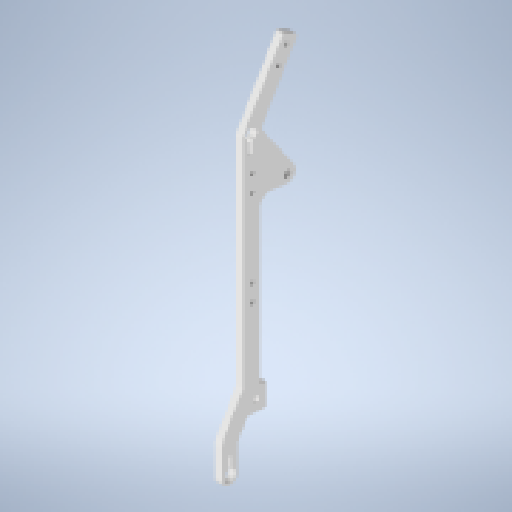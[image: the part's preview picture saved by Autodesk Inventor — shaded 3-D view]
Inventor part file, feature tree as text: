
AUTODESK INVENTOR PART (.ipt)
format: ipt  version: 2024 (Build 280153000, 153)  size: 407,040 bytes
history: native  units: mm
features: sketch x8, fillet x6, extrude x5, hole x5, projected_geometry x3, thicken_offset x1, other x1
ambient origin geometry x8: Origin, YZ Plane, XZ Plane, XY Plane, X Axis, Y Axis, Z Axis, Center Point
bodies: Solid1 (feature_tree)
feature tree (29):
  sketch  "Sketch1"  dims[d0=270.0mm d1=20.0mm d4=20.0mm]
  thicken_offset  "Thicken1"
  sketch  "Sketch2"  dims[d5=20.0mm d9=6.35mm d10=0.0mm]
  extrude  "Extrusion1"  Depth=20.0mm
  fillet  "Fillet1"  Radius=20.0mm
  hole  "Hole2"  [1 undecoded]
  hole  "Hole3"  [1 undecoded]
  extrude  "Extrusion2"  Depth=15.0mm
  fillet  "Fillet2"  Radius=3.0mm
  hole  "Hole4"  [1 undecoded]
  fillet  "Fillet5"  Radius=20.0mm
  extrude  "Extrusion3"  Depth=8.0mm
  fillet  "Fillet4"  Radius=16.0mm
  hole  "Hole6"  [1 undecoded]
  extrude  "Extrusion4"  Depth=10.0mm
  fillet  "Fillet6"  Radius=10.0mm
  fillet  "Fillet7"  Radius=28.0mm
  hole  "Hole7"  [1 undecoded]
  other  "Srf1"
  sketch  "Sketch4"  dims[d14=16.0mm d33=6.35mm d34=0.0mm]
  sketch  "Sketch5"  dims[d38=1.0mm]
  sketch  "Sketch6"  dims[d42=5.3mm d43=6.0mm d44=4.0mm d45=2.0mm d46=90.0deg d47=8.0mm d48=20.594885mm]
  projected_geometry  "Projected Loop7"
  sketch  "Sketch8"  dims[d49=11.05mm d50=6.0mm d51=4.0mm d52=2.0mm d53=90.0deg d54=8.0mm d55=20.594885mm d63=15.0mm d64=3.0mm]
  sketch  "Sketch9"  dims[d65=0.0mm d66=0.0mm d67=1.0mm d75=20.0mm]
  projected_geometry  "Projected Loop8"
  sketch  "Sketch10"  dims[d76=20.0mm d78=50.0mm d91=4.134mm d92=10.0mm d93=4.0mm d94=2.0mm d95=90.0deg d96=8.0mm d97=20.594885mm d98=16.0mm d101=10.0mm d102=0.0mm d103=10.0mm d112=10.0mm d113=28.0mm d114=150.0deg d116=15.0mm d118=9.0mm d119=3.0mm d121=3.0mm d122=13.962634mm d123=60.0mm d124=6.108652mm d125=6.4008mm d126=15.875mm d127=4.0mm d128=2.0mm d129=90.0deg d130=8.0mm d131=20.594885mm d132=180.0mm d133=16.0mm d134=9.0mm d135=90.0mm d146=10.0mm d147=0.0mm d148=2.0mm d149=150.0deg d150=80.0mm d151=2.0mm d152=20.0mm d153=4.6mm d154=18.0mm d155=8.0mm d156=8.0mm d157=4.134mm d158=10.0mm d159=4.0mm d160=2.0mm d161=90.0deg d162=8.0mm d163=20.594885mm d74=0.0mm d77=0.0mm]
  projected_geometry  "Projected Loop9"
  extrude  "ExtrusionSrf1"  Depth=15.0mm
note: 5 required parameter values undecoded (feature->parameter linkage not recoverable at this tier; creation-order binding heuristic only, values carry confidence <= 0.55)
